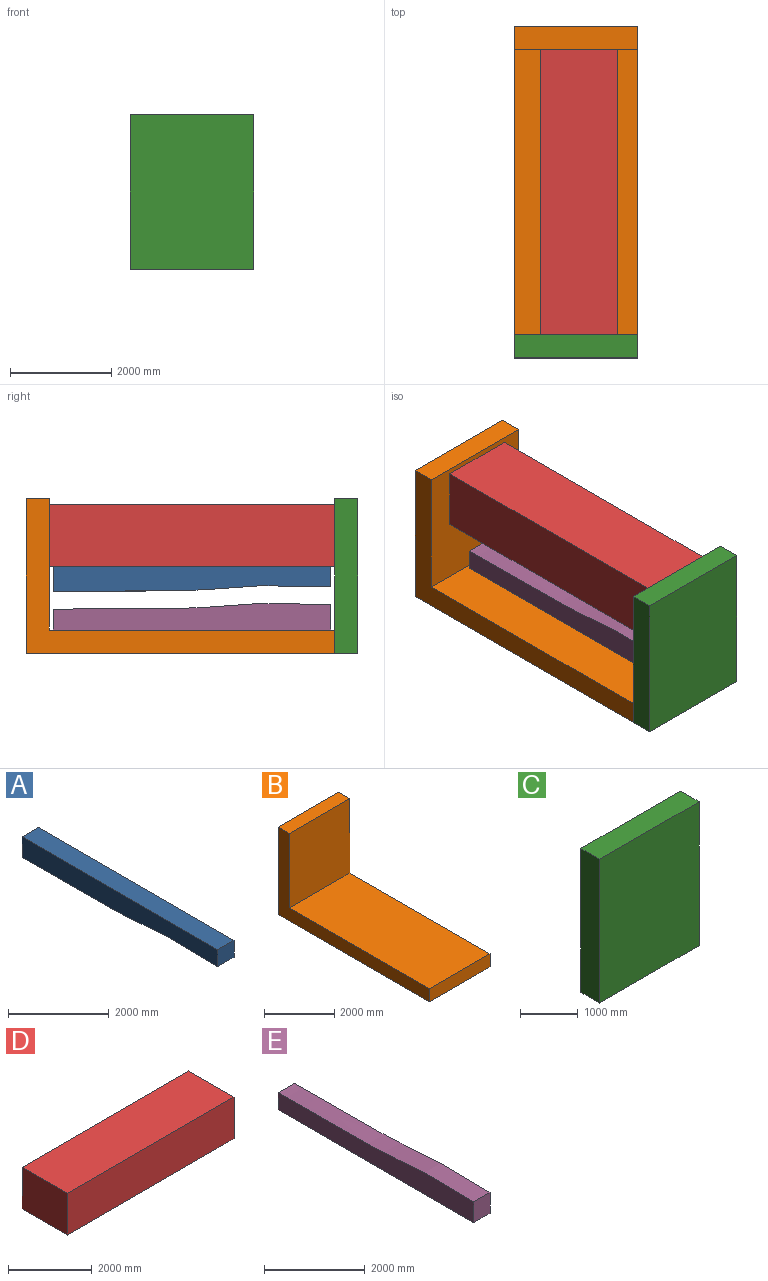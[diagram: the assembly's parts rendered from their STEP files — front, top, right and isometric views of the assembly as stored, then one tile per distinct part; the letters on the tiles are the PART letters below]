
ASSEMBLY  parts=5 mates=4
PART A: 6 faces, bbox 457.2x5486.4x520.5 mm
  f0: plane 457.2x409.92mm, normal (0,-1,0), area 187414.4mm2, adj f1,f3,f4,f5
  f1: extruded ~5486.4x457.2mm, area 2509468.1mm2, adj f0,f2,f4,f5
  f2: plane 501.83x457.2mm, normal (0,1,0), area 229438.7mm2, adj f1,f3,f4,f5
  f3: plane 5486.4x457.2mm, normal (0,0,1), area 2508382.1mm2, adj f0,f2,f4,f5
  f4: plane 5486.4x520.5mm, normal (1,0,0), area 2487818mm2, adj f0,f1,f2,f3
  f5: plane 5486.4x520.5mm, normal (-1,0,0), area 2487818mm2, adj f0,f1,f2,f3
PART B: 8 faces, bbox 2438.4x6096x3048 mm
  f0: plane 2590.8x2438.4mm, normal (0,-1,0), area 6317406.7mm2, adj f1,f2,f4,f7
  f1: plane 6096x3048mm, normal (-1,0,0), area 3971605mm2, adj f0,f3,f4,f5,f6,f7
  f2: plane 6096x3048mm, normal (1,0,0), area 3971605mm2, adj f0,f3,f4,f5,f6,f7
  f3: plane 3048x2438.4mm, normal (0,1,0), area 7432243.2mm2, adj f1,f2,f4,f5
  f4: plane 2438.4x457.2mm, normal (0,0,1), area 1114836.5mm2, adj f0,f1,f2,f3
  f5: plane 6096x2438.4mm, normal (0,0,-1), area 14864486.4mm2, adj f1,f2,f3,f6
  f6: plane 2438.4x457.2mm, normal (0,-1,0), area 1114836.5mm2, adj f1,f2,f5,f7
  f7: plane 5638.8x2438.4mm, normal (0,0,1), area 13749649.9mm2, adj f0,f1,f2,f6
PART C: 6 faces, bbox 2438.4x457.2x3048 mm
  f0: plane 3048x457.2mm, normal (-1,0,0), area 1393545.6mm2, adj f1,f3,f4,f5
  f1: plane 3048x2438.4mm, normal (0,-1,0), area 7432243.2mm2, adj f0,f2,f4,f5
  f2: plane 3048x457.2mm, normal (1,0,0), area 1393545.6mm2, adj f1,f3,f4,f5
  f3: plane 3048x2438.4mm, normal (0,1,0), area 7432243.2mm2, adj f0,f2,f4,f5
  f4: plane 2438.4x457.2mm, normal (0,0,1), area 1114836.5mm2, adj f0,f1,f2,f3
  f5: plane 2438.4x457.2mm, normal (0,0,-1), area 1114836.5mm2, adj f0,f1,f2,f3
PART D: 6 faces, bbox 5638.8x1524x1219.2 mm
  f0: plane 1524x1219.2mm, normal (-1,0,0), area 1858060.8mm2, adj f1,f3,f4,f5
  f1: plane 5638.8x1219.2mm, normal (0,-1,0), area 6874825mm2, adj f0,f2,f4,f5
  f2: plane 1524x1219.2mm, normal (1,0,0), area 1858060.8mm2, adj f1,f3,f4,f5
  f3: plane 5638.8x1219.2mm, normal (0,1,0), area 6874825mm2, adj f0,f2,f4,f5
  f4: plane 5638.8x1524mm, normal (0,0,1), area 8593531.2mm2, adj f0,f1,f2,f3
  f5: plane 5638.8x1524mm, normal (0,0,-1), area 8593531.2mm2, adj f0,f1,f2,f3
PART E: 6 faces, bbox 457.2x5486.4x534.9 mm
  f0: plane 5486.4x457.2mm, normal (0,0,-1), area 2508382.1mm2, adj f1,f3,f4,f5
  f1: plane 457.2x412.57mm, normal (0,1,0), area 188625mm2, adj f0,f2,f4,f5
  f2: extruded ~5486.4x457.2mm, area 2509468.1mm2, adj f1,f3,f4,f5
  f3: plane 504.48x457.2mm, normal (0,-1,0), area 230649.2mm2, adj f0,f2,f4,f5
  f4: plane 5486.4x534.87mm, normal (1,0,0), area 2528946.2mm2, adj f0,f1,f2,f3
  f5: plane 5486.4x534.87mm, normal (-1,0,0), area 2528946.2mm2, adj f0,f1,f2,f3
PLACE A t=(-1393.72,533.4,806.34)mm
PLACE B t=(-2438.4,0,0)mm
PLACE C t=(-2438.4,0,0)mm
PLACE D rot(axis=(0,0,1),90deg) t=(-403.12,457.2,1720.74)mm
PLACE E t=(-1447.8,533.4,457.2)mm
MATE fastened A.f3 <-> D.f5  axis (0,0,1) through (-1165.12,3276.6,1720.74)mm
MATE fastened E.f0 <-> B.f7  axis (0,0,-1) through (-1219.2,3276.6,457.2)mm
MATE planar C.f3 <-> D.f0  axis (0,1,0) through (-1219.2,457.2,1524)mm
MATE fastened B.f5 <-> C.f5  axis (0,0,1) through (0,457.2,0)mm
